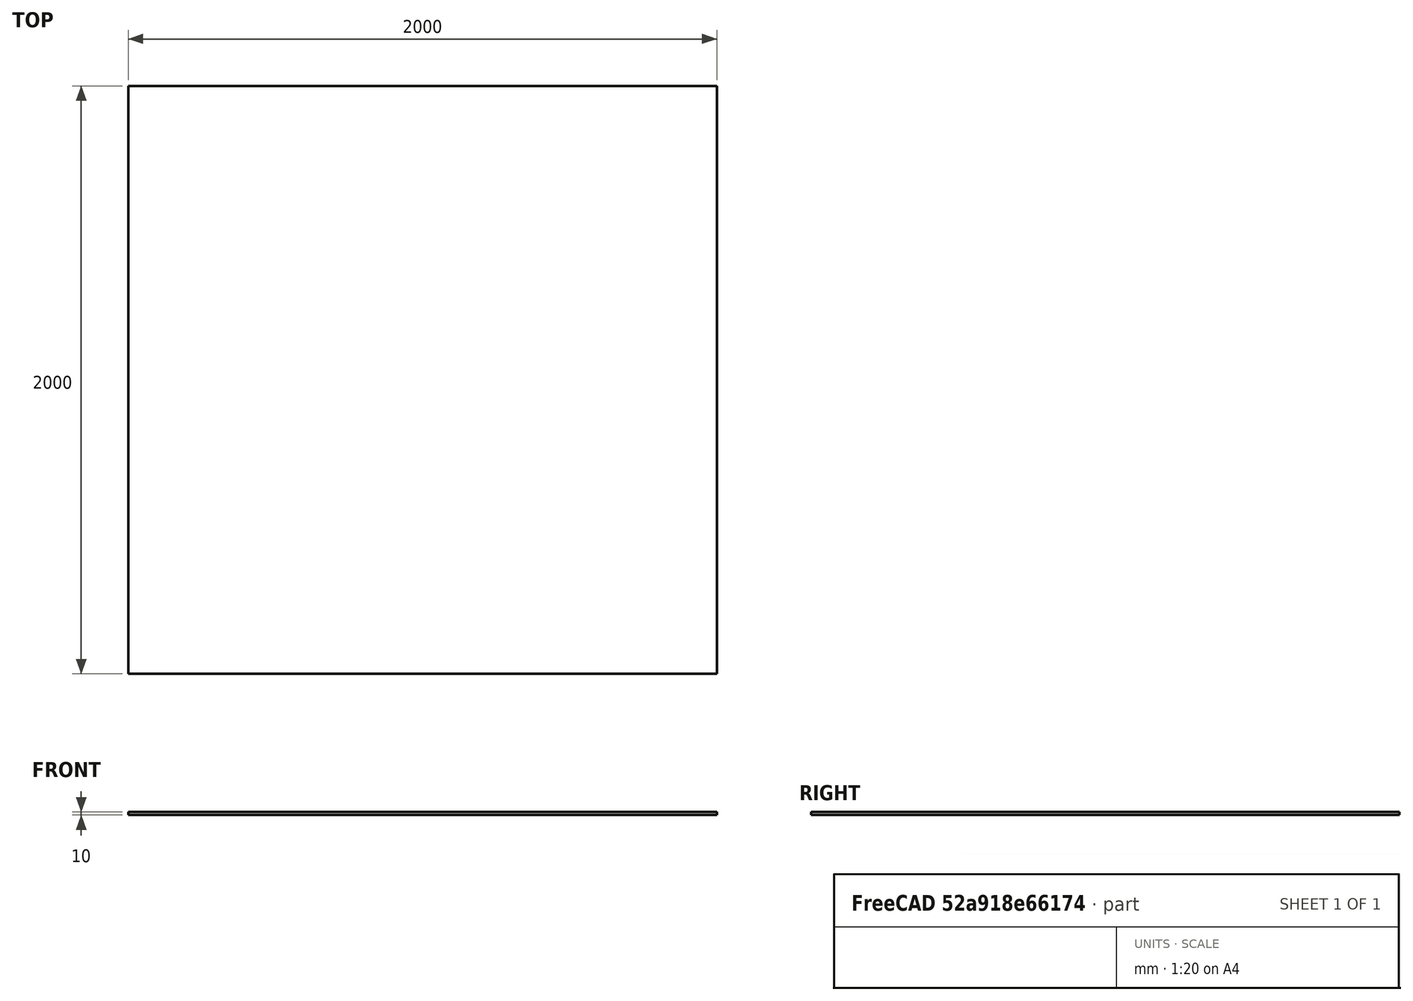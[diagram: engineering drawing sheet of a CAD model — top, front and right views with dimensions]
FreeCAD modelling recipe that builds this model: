
FCSTD DOCUMENT  (FreeCAD 0.18.4R)
Label: base
License: All rights reserved
LicenseURL: http://en.wikipedia.org/wiki/All_rights_reserved
objects: Sketcher::SketchObject×1, PartDesign::Pad×1, PartDesign::Body×1
note: 4 computed .brp shape members not serialized (recipe doc carries the construction recipe); baked Part::Feature solids carry a one-line shape summary decoded from their .brp

FEATURE [Sketcher::SketchObject] Sketch
  MapMode = 5
  Support = -> [XY_Plane]
  sketch-geometry (4):
    g0: LineSegment StartX=-1000 StartY=1000 StartZ=0 EndX=1000 EndY=1000 EndZ=0
    g1: LineSegment StartX=1000 StartY=1000 StartZ=0 EndX=1000 EndY=-1000 EndZ=0
    g2: LineSegment StartX=1000 StartY=-1000 StartZ=0 EndX=-1000 EndY=-1000 EndZ=0
    g3: LineSegment StartX=-1000 StartY=-1000 StartZ=0 EndX=-1000 EndY=1000 EndZ=0
  constraints (12):
    c: Coincident(g0,g1)
    c: Coincident(g1,g2)
    c: Coincident(g2,g3)
    c: Coincident(g3,g0)
    c: Horizontal(g0)
    c: Horizontal(g2)
    c: Vertical(g1)
    c: Vertical(g3)
    c: DistanceX(g0,g-1) = 1000
    c: DistanceY(g1,g-1) = 1000
    c: DistanceY(g-1,g0) = 1000
    c: DistanceX(g-1,g1) = 1000
FEATURE [PartDesign::Pad] Pad
  Length = 10
  Length2 = 100
  Midplane = true
  Profile = -> Sketch
  Type = 0
FEATURE [PartDesign::Body] Body
  Group = -> [Sketch,Pad]
  Origin = -> Origin
  Tip = -> Pad
